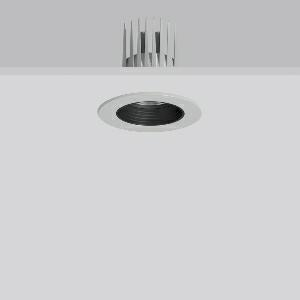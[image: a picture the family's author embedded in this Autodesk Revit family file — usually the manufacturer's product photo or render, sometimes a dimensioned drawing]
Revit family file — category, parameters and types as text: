
# Revit family: heledon_mini_e_901744_004_3_76_ec2c
name_source: partatom
category: Lighting Fixtures
units: mm (PartAtom-declared; Revit-internal decimal feet)

## family parameters
Cut with Voids When Loaded = No
Host = Face
Light Source = No
Part Type = Normal
Room Calculation Point = No
Round Connector Dimension = Use Diameter
Shared = No

## types (1)
- HELEDON mini E (1 x LED Modul 935, 2150 lm, 3500)
    Apparent Load = 20 VA
    Approval mark = CE
    CIE Flux Codes = 96 100 100 100 100
    Color Rendering = 92
    Color Temperature = 3500
    Default Elevation = 1800 mm
    Description = Series: HELEDON mini
Round recessed downlight. Housing: die-cast aluminium, powder-coated. Black plastic ring and recessed LED to prevent glare from the side. Optical assembly with lens made of plastic (polycarbonate) for the best homogeneous light distribution - can be changed without tools. Best colour rendering index Ra>90. Suitable for Recessed ceiling mounting. Installation without tools thanks to spring fastening system. Including separate LED converter with connecting cable 600 mm.High quality converter without flickering and stroboscopic effect. Through-wiring box (5 pole) available as accessory. The following accessories can be mounted without use of tools: interchangeable lenses, decorative glasses, honeycomb louvre, clear and frosted diffusers, white interchangeable plastic ring. 
Colour: silver
Diameter: 124 mm
Height: 3 mm
Cut-out diameter: 114 mm
Recess height: 170 mm
Luminaire: recess height: 120 mm
Lamp: LED
Socket: without socket
Colour temperature: 3500K
Colour rendering index (CRI): 92
System power: 20 W
Rated luminous flux: 2150 lm
Luminous efficiency: 108 lm/W
Control gear: Converter, dimmable, DALI
Protection class: II
Type of protection: IP 20
    Height = 0 mm  [stored 0 ft]
    Lamp = 1 x LED Modul 935
    Lamp Light Flux = 2150 lm
    Lamp count = 1
    Length = 124 mm  [stored 0.406824 ft]
    Lifetime = 50000 h
    Luminous efficacy = 108 lm/W
    Manufacturer = RZB
    ModVariant = No
    Model = 901744.004.3.76
    Mounting Place = Ceiling
    Mounting Type = Recessed
    Number of Poles = 1
    OnlyDefault = Yes
    Power Factor = 1
    Product Name = HELEDON mini E
    Product group = Recessed downlights
    ProductGroupID = 402
    Protection Class = Protection class II
    Protection Degree = IP 20
    RLX_Detail_Level = 1
    RLX_Emergency_Light_Flux = 0 lm
    RLX_Emergency_Type = 0
    RLX_Emergency_Type_DB = No
    RlxData = <blob elided: 126837 chars, md5=31d8c3ad>
    Socket = socket
    Standby Power = 0 W
    System Light Flux = 2150 lm
    System Power = 20 W
    Type Comments = Product without accessories
    Type Image = 901656.004.jpg
    URL = http://relux.com
    VarID = ---
    Voltage = 230 V
    Voltage Range = 220-240 V
    Weight = 0.00 kg
    Width = 0 mm  [stored 0 ft]

note: [stored X ft] marks values corroborated as IEEE doubles in the binary element streams (Revit-internal decimal feet)

## geometry (parser evidence)
native form markers: Blend x4, Sweep x12
no freeform markers — native parametric forms only
